# Revit family: Duplo-Schrauböse mit Innengewinde
name_source: partatom
category: HLS-Bauteile
revit_build: Autodesk Revit 2017 (Build: 20190507_1515(x64)
units: mm (PartAtom-declared; Revit-internal decimal feet)

## family parameters
Arbeitsebenenbasiert = Nein
Beim Laden mit Abzugskörper schneiden = Nein
Bemaßung runder Anschluss = Durchmesser verwenden
Gemeinsam genutzt = Ja
Immer vertikal = Nein
Raumberechnungspunkt = Nein
Teiletyp = Normal

## types (2) — shared parameters
B = 18 mm
D = 9 mm  [stored 0.0295276 ft]
Fabrikat = MEFA
Firma = MEFA Befestigungs- und Montagesysteme GmbH
Gewicht = 0.02 kg
Gewicht pro Bauteil = 0.02 kg
Kurztext1 = Schrauböse Duplo
L = 38 mm  [stored 0.124672 ft]
L1 = 10 mm  [stored 0.0328084 ft]
Lochdurchmesser = 9 mm
Material = Zinkguss
Mengeneinheit = St
Oberflaeche = blank
S = 4 mm  [stored 0.0131234 ft]
vpe = 100 St
zero-valued in all types: Länge, Länge Gewinde

## per-type parameters (varying)
| type | Artikelnummer | EAN | Kurztext2 | M |
| Duplo-Schrauböse mit Innengewinde  M 6 | 0350133 | 4250928407696 | Innengewinde M6 Lochung 9 mm | 6 mm  [stored 0.019685 ft] |
| Duplo-Schrauböse mit Innengewinde  M 8 | 0350141 | 4250928407702 | Innengewinde M8 Lochung 9 mm | 8 mm  [stored 0.0262467 ft] |

note: [stored X ft] marks values corroborated as IEEE doubles in the binary element streams (Revit-internal decimal feet)
